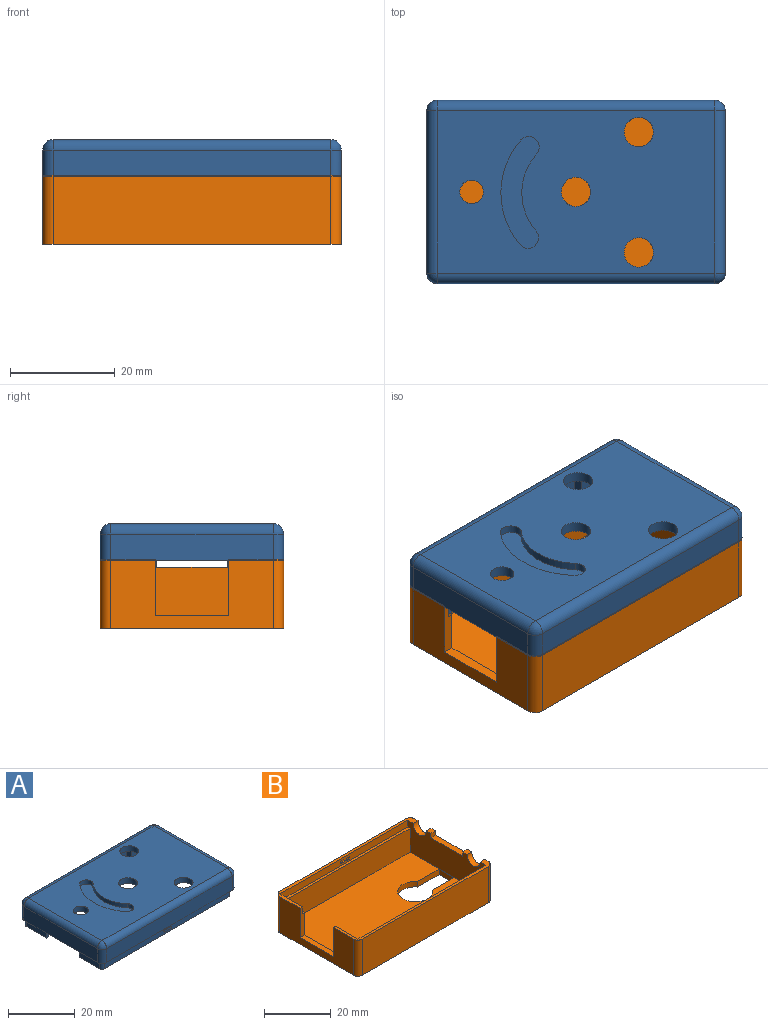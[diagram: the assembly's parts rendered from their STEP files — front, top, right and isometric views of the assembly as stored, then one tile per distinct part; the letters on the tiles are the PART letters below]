
ASSEMBLY  parts=2 mates=1
PART A: 108 faces, bbox 57x35x9.8 mm
  f0: plane 8.52x2.8mm, normal (-1,0,0), area 23.8mm2, adj f1,f6,f105,f106
  f1: plane 54.02x9.52mm, normal (0,0,-1), area 62.3mm2, adj f0,f2,f3,f4,f80,f105,f106
  f2: plane 8.52x2.8mm, normal (1,0,0), area 23.8mm2, adj f1,f4,f6,f106
  f3: plane 54.74x2.8mm, normal (0,-1,0), area 146.2mm2, adj f1,f6,f79,f80,f92,f99,f100,f101
  f4: plane 55.02x2.8mm, normal (0,1,0), area 148.4mm2, adj f1,f2,f6,f79,f80
  f5: plane 54.02x9.52mm, normal (0,0,-1), area 62.3mm2, adj f75,f76,f77,f78,f93,f104,f107
  f6: plane 57x35mm, normal (0,0,-1), area 165.2mm2, adj f0,f2,f3,f4,f7,f9,f10,f11
  f7: plane 8.1x5.03mm, normal (0,1,0), area 40.7mm2, adj f6,f8,f17,f73
  f8: plane 53x31mm, normal (0,0,-1), area 1497.2mm2, adj f7,f9,f14,f15,f16,f17,f23,f24
  f9: plane 37.41x5.03mm, normal (0,1,0), area 188.1mm2, adj f6,f8,f31,f71
  f10: plane 31x5.03mm, normal (-1,0,0), area 155.9mm2, adj f6,f81,f83,f84
  f11: plane 53x5.03mm, normal (0,1,0), area 266.5mm2, adj f6,f81,f85,f86
  f12: plane 53x5.03mm, normal (0,-1,0), area 266.5mm2, adj f6,f83,f89,f92
  f13: plane 31.01x5.04mm, normal (1,0,0), area 69.7mm2, adj f6,f18,f19,f20,f21,f27,f28,f29
  f14: plane 53x5.03mm, normal (0,-1,0), area 266.5mm2, adj f6,f8,f15,f17
  f15: plane 31x5.03mm, normal (1,0,0), area 155.9mm2, adj f6,f8,f14,f16
  f16: plane 5.03x0.48mm, normal (0,1,0), area 2.4mm2, adj f6,f8,f15,f32
  f17: plane 31x5.03mm, normal (-1,0,0), area 69.7mm2, adj f6,f7,f8,f14,f18,f19,f20,f21
  f18: cylinder r=2.75mm len=5.5mm, axis (1,0,0), area 17.8mm2, adj f6,f13,f17,f29
  f19: cylinder r=2.75mm len=5.5mm, axis (1,0,0), area 17.7mm2, adj f6,f13,f17,f28
  f20: plane 4.53x2mm, normal (0,1,0), area 9.1mm2, adj f13,f17,f27,f29
  f21: plane 4.53x2mm, normal (0,-1,0), area 9.1mm2, adj f13,f17,f27,f28
  f22: plane 53x31mm, normal (0,0,1), area 1464.7mm2, adj f23,f24,f25,f26,f55,f56,f57,f58
  f23: cylinder r=2.8mm len=5.6mm, axis (0,0,1), area 35.2mm2, adj f8,f22
  f24: cylinder r=2.8mm len=5.6mm, axis (0,0,1), area 35.2mm2, adj f8,f22
  f25: cylinder r=2.8mm len=5.6mm, axis (0,0,1), area 35.2mm2, adj f8,f22
  f26: cylinder r=2.25mm len=4.5mm, axis (0,0,1), area 28.3mm2, adj f8,f22
  f27: plane 13.5x2mm, normal (0,0,-1), area 27mm2, adj f13,f17,f20,f21
  f28: plane 2x1.87mm, normal (0,0,-1), area 3.7mm2, adj f13,f17,f19,f21
  f29: plane 2x1.88mm, normal (0,0,-1), area 3.8mm2, adj f13,f17,f18,f20
  f30: plane 3.5x1.77mm, normal (0,-1,0), area 6.2mm2, adj f6,f31,f32,f34
  f31: plane 6.8x2mm, normal (1,0,0), area 13.6mm2, adj f8,f9,f30,f33,f34
  f32: plane 6.8x2mm, normal (-1,0,0), area 13.6mm2, adj f8,f16,f30,f33,f34
  f33: plane 6.8x3.5mm, normal (0,1,0), area 23.8mm2, adj f8,f31,f32,f34
  f34: plane 3.5x2mm, normal (0,0,-1), area 7mm2, adj f30,f31,f32,f33
  f35: plane 6.8x2mm, normal (1,0,0), area 13.6mm2, adj f8,f36,f38,f39
  f36: plane 6.8x3.5mm, normal (0,-1,0), area 23.8mm2, adj f8,f35,f37,f39
  f37: plane 6.8x2mm, normal (-1,0,0), area 13.6mm2, adj f8,f36,f38,f39
  f38: plane 6.8x3.5mm, normal (0,1,0), area 23.8mm2, adj f8,f35,f37,f39
  f39: plane 3.5x2mm, normal (0,0,-1), area 7mm2, adj f35,f36,f37,f38
  f40: plane 6.8x2mm, normal (1,0,0), area 13.6mm2, adj f8,f41,f43,f44
  f41: plane 6.8x3.5mm, normal (0,-1,0), area 23.8mm2, adj f8,f40,f42,f44
  f42: plane 6.8x2mm, normal (-1,0,0), area 13.6mm2, adj f8,f41,f43,f44
  f43: plane 6.8x3.5mm, normal (0,1,0), area 23.8mm2, adj f8,f40,f42,f44
  f44: plane 3.5x2mm, normal (0,0,-1), area 7mm2, adj f40,f41,f42,f43
  f45: plane 6.8x2mm, normal (-1,0,0), area 13.6mm2, adj f8,f46,f48,f49
  f46: plane 6.8x3.5mm, normal (0,1,0), area 23.8mm2, adj f8,f45,f47,f49
  f47: plane 6.8x2mm, normal (1,0,0), area 13.6mm2, adj f8,f46,f48,f49
  f48: plane 6.8x3.5mm, normal (0,-1,0), area 23.8mm2, adj f8,f45,f47,f49
  f49: plane 3.5x2mm, normal (0,0,-1), area 7mm2, adj f45,f46,f47,f48
  f50: plane 6.8x3.5mm, normal (0,1,0), area 23.8mm2, adj f8,f51,f53,f54
  f51: plane 6.8x2mm, normal (1,0,0), area 13.6mm2, adj f8,f50,f52,f54
  f52: plane 6.8x3.5mm, normal (0,-1,0), area 23.8mm2, adj f8,f51,f53,f54
  f53: plane 6.8x2mm, normal (-1,0,0), area 13.6mm2, adj f8,f50,f52,f54
  f54: plane 3.5x2mm, normal (0,0,-1), area 7mm2, adj f50,f51,f52,f53
  f55: cylinder r=11.14mm len=14.73mm, axis (0,0,1), area 24.1mm2, adj f22,f56,f58,f59
  f56: cylinder r=2mm len=3.49mm, axis (0,0,1), area 9.4mm2, adj f22,f55,f57,f59
  f57: cylinder r=15.14mm len=20.02mm, axis (0,0,1), area 32.8mm2, adj f22,f56,f58,f59
  f58: cylinder r=2mm len=3.51mm, axis (0,0,1), area 9.4mm2, adj f22,f55,f57,f59
  f59: plane 21.37x7.34mm, normal (0,0,1), area 88.5mm2, adj f55,f56,f57,f58
  f60: plane 6.8x2mm, normal (-1,0,0), area 13.6mm2, adj f8,f61,f63,f64
  f61: plane 6.8x3.5mm, normal (0,1,0), area 23.8mm2, adj f8,f60,f62,f64
  f62: plane 6.8x2mm, normal (1,0,0), area 13.6mm2, adj f8,f61,f63,f64
  f63: plane 6.8x3.5mm, normal (0,-1,0), area 23.8mm2, adj f8,f60,f62,f64
  f64: plane 3.5x2mm, normal (0,0,-1), area 7mm2, adj f60,f61,f62,f63
  f65: plane 6.8x2mm, normal (-1,0,0), area 13.6mm2, adj f8,f66,f68,f69
  f66: plane 6.8x3.5mm, normal (0,1,0), area 23.8mm2, adj f8,f65,f67,f69
  f67: plane 6.8x2mm, normal (1,0,0), area 13.6mm2, adj f8,f66,f68,f69
  f68: plane 6.8x3.5mm, normal (0,-1,0), area 23.8mm2, adj f8,f65,f67,f69
  f69: plane 3.5x2mm, normal (0,0,-1), area 7mm2, adj f65,f66,f67,f68
  f70: plane 3.5x1.77mm, normal (0,-1,0), area 6.2mm2, adj f6,f71,f73,f74
  f71: plane 6.8x2mm, normal (-1,0,0), area 13.6mm2, adj f8,f9,f70,f72,f74
  f72: plane 6.8x3.5mm, normal (0,1,0), area 23.8mm2, adj f8,f71,f73,f74
  f73: plane 6.8x2mm, normal (1,0,0), area 13.6mm2, adj f7,f8,f70,f72,f74
  f74: plane 3.5x2mm, normal (0,0,-1), area 7mm2, adj f70,f71,f72,f73
  f75: plane 53.02x2.8mm, normal (0,1,0), area 146.1mm2, adj f5,f6,f93,f94,f95,f96,f97,f104
  f76: plane 53.02x2.8mm, normal (0,-1,0), area 148.4mm2, adj f5,f6,f77,f93
  f77: plane 8.52x2.8mm, normal (1,0,0), area 23.8mm2, adj f5,f6,f76,f107
  f78: plane 8.52x2.8mm, normal (-1,0,0), area 23.8mm2, adj f5,f6,f104,f107
  f79: plane 2.01x1.01mm, normal (0,0,-1), area 1.9mm2, adj f3,f4,f80,f92
  f80: plane 2.77x1mm, normal (1,0,0), area 2.8mm2, adj f1,f3,f4,f79
  f81: cylinder r=2mm len=5.03mm, axis (0,0,-1), area 15.8mm2, adj f6,f10,f11,f82
  f82: sphere r=2mm, area 6.3mm2, adj f81,f84,f85
  f83: cylinder r=2mm len=5.03mm, axis (0,0,1), area 15.8mm2, adj f6,f10,f12,f87
  f84: cylinder r=2mm len=31mm, axis (0,1,0), area 97.4mm2, adj f10,f22,f82,f87
  f85: cylinder r=2mm len=53mm, axis (1,0,0), area 166.5mm2, adj f11,f22,f82,f88
  f86: cylinder r=2mm len=5.03mm, axis (0,0,1), area 15.8mm2, adj f6,f11,f13,f88
  f87: sphere r=2mm, area 8.6mm2, adj f83,f84,f89
  f88: sphere r=2mm, area 6.3mm2, adj f85,f86,f90
  f89: cylinder r=2mm len=53mm, axis (-1,0,0), area 166.5mm2, adj f12,f22,f87,f91
  f90: cylinder r=2mm len=31mm, axis (0,-1,0), area 97.4mm2, adj f13,f22,f88,f91
  f91: sphere r=2mm, area 4mm2, adj f89,f90,f92
  f92: cylinder r=2mm len=5.05mm, axis (0,0,-1), area 15.8mm2, adj f3,f6,f12,f13,f79,f91
  f93: plane 2.8x1mm, normal (1,0,0), area 2.8mm2, adj f5,f6,f75,f76
  f94: plane 0.75x0.3mm, normal (1,0,0), area 0.2mm2, adj f75,f95,f97,f98
  f95: plane 3x0.3mm, normal (0,0,-1), area 0.9mm2, adj f75,f94,f96,f98
  f96: plane 0.75x0.3mm, normal (-1,0,0), area 0.2mm2, adj f75,f95,f97,f98
  f97: plane 3x0.3mm, normal (0,0,1), area 0.9mm2, adj f75,f94,f96,f98
  f98: plane 3x0.75mm, normal (0,1,0), area 2.2mm2, adj f94,f95,f96,f97
  f99: plane 0.75x0.3mm, normal (-1,0,0), area 0.2mm2, adj f3,f100,f102,f103
  f100: plane 3x0.3mm, normal (0,0,-1), area 0.9mm2, adj f3,f99,f101,f103
  f101: plane 0.75x0.3mm, normal (1,0,0), area 0.2mm2, adj f3,f100,f102,f103
  f102: plane 3x0.3mm, normal (0,0,1), area 0.9mm2, adj f3,f99,f101,f103
  f103: plane 3x0.75mm, normal (0,-1,0), area 2.3mm2, adj f99,f100,f101,f102
  f104: cylinder r=1mm len=2.8mm, axis (0,0,-1), area 4.4mm2, adj f5,f6,f75,f78
  f105: cylinder r=1mm len=2.8mm, axis (0,0,-1), area 4.4mm2, adj f0,f1,f3,f6
  f106: plane 2.8x1mm, normal (0,1,0), area 2.8mm2, adj f0,f1,f2,f6
  f107: plane 2.8x1mm, normal (0,-1,0), area 2.8mm2, adj f5,f6,f77,f78
PART B: 46 faces, bbox 57x35x13.2 mm
  f0: plane 54x2.5mm, normal (0,-1,0), area 131.5mm2, adj f5,f8,f28,f29,f41,f42,f43,f44
  f1: plane 54x2.5mm, normal (0,1,0), area 131.5mm2, adj f3,f8,f30,f31,f36,f37,f38,f39
  f2: plane 10.75x2mm, normal (0,1,0), area 19mm2, adj f3,f7,f13,f23,f30,f31
  f3: plane 57x10.5mm, normal (0,0,1), area 69.5mm2, adj f1,f2,f7,f8,f9,f11,f16,f30
  f4: plane 10.75x2mm, normal (0,-1,0), area 19mm2, adj f5,f7,f13,f23,f28,f29
  f5: plane 57x10.5mm, normal (0,0,1), area 69.5mm2, adj f0,f4,f7,f8,f10,f11,f15,f28
  f6: plane 57x35mm, normal (0,0,-1), area 1852.5mm2, adj f7,f9,f10,f11,f24,f25,f26,f27
  f7: plane 31x13.23mm, normal (-1,0,0), area 259.6mm2, adj f2,f3,f4,f5,f6,f23,f33,f34
  f8: plane 33x11.23mm, normal (-1,0,0), area 307.4mm2, adj f0,f1,f3,f5,f12,f14,f15,f16
  f9: plane 53x13.23mm, normal (0,-1,0), area 701.1mm2, adj f3,f6,f32,f33
  f10: plane 53x13.23mm, normal (0,1,0), area 701.1mm2, adj f5,f6,f34,f35
  f11: plane 31x13.23mm, normal (1,0,0), area 364.4mm2, adj f3,f5,f6,f15,f16,f17,f18,f20
  f12: plane 53x8.73mm, normal (0,1,0), area 462.6mm2, adj f8,f13,f19,f31
  f13: plane 31x8.73mm, normal (1,0,0), area 155.1mm2, adj f2,f4,f12,f14,f19,f23,f29,f31
  f14: plane 53x8.73mm, normal (0,-1,0), area 462.6mm2, adj f8,f13,f19,f29
  f15: cylinder r=2.75mm len=5.5mm, axis (1,0,0), area 17.8mm2, adj f5,f8,f11,f22
  f16: cylinder r=2.75mm len=5.5mm, axis (1,0,0), area 17.7mm2, adj f3,f8,f11,f21
  f17: plane 2x1.53mm, normal (0,-1,0), area 3.1mm2, adj f8,f11,f20,f22
  f18: plane 2x1.53mm, normal (0,1,0), area 3.1mm2, adj f8,f11,f20,f21
  f19: plane 53x31mm, normal (0,0,1), area 1503.9mm2, adj f8,f12,f13,f14,f24,f25,f26,f27
  f20: plane 13.5x2mm, normal (0,0,1), area 27mm2, adj f8,f11,f17,f18
  f21: plane 2x1.87mm, normal (0,0,1), area 3.7mm2, adj f8,f11,f16,f18
  f22: plane 2x1.88mm, normal (0,0,1), area 3.8mm2, adj f8,f11,f15,f17
  f23: plane 14x2mm, normal (0,0,1), area 28mm2, adj f2,f4,f7,f13
  f24: cylinder r=5.25mm len=10.5mm, axis (0,0,1), area 52.5mm2, adj f6,f19,f25,f26
  f25: plane 9.05x2mm, normal (0,-1,0), area 18.1mm2, adj f6,f19,f24,f27
  f26: plane 9.05x2mm, normal (0,1,0), area 18.1mm2, adj f6,f19,f24,f27
  f27: plane 6.3x2mm, normal (-1,0,0), area 12.6mm2, adj f6,f19,f25,f26
  f28: plane 9.5x2.5mm, normal (1,0,0), area 23.8mm2, adj f0,f4,f5,f29
  f29: plane 54x9.5mm, normal (0,0,1), area 62.5mm2, adj f0,f4,f8,f13,f14,f28
  f30: plane 9.5x2.5mm, normal (1,0,0), area 23.8mm2, adj f1,f2,f3,f31
  f31: plane 54x9.5mm, normal (0,0,1), area 62.5mm2, adj f1,f2,f8,f12,f13,f30
  f32: cylinder r=2mm len=13.23mm, axis (0,0,-1), area 41.6mm2, adj f3,f6,f9,f11
  f33: cylinder r=2mm len=13.23mm, axis (0,0,1), area 41.6mm2, adj f3,f6,f7,f9
  f34: cylinder r=2mm len=13.23mm, axis (0,0,-1), area 41.6mm2, adj f5,f6,f7,f10
  f35: cylinder r=2mm len=13.23mm, axis (0,0,1), area 41.6mm2, adj f5,f6,f10,f11
  f36: plane 1x0.4mm, normal (1,0,0), area 0.4mm2, adj f1,f37,f39,f40
  f37: plane 3.5x0.4mm, normal (0,0,-1), area 1.4mm2, adj f1,f36,f38,f40
  f38: plane 1x0.4mm, normal (-1,0,0), area 0.4mm2, adj f1,f37,f39,f40
  f39: plane 3.5x0.4mm, normal (0,0,1), area 1.4mm2, adj f1,f36,f38,f40
  f40: plane 3.5x1mm, normal (0,1,0), area 3.5mm2, adj f36,f37,f38,f39
  f41: plane 1x0.4mm, normal (-1,0,0), area 0.4mm2, adj f0,f42,f44,f45
  f42: plane 3.5x0.4mm, normal (0,0,-1), area 1.4mm2, adj f0,f41,f43,f45
  f43: plane 1x0.4mm, normal (1,0,0), area 0.4mm2, adj f0,f42,f44,f45
  f44: plane 3.5x0.4mm, normal (0,0,1), area 1.4mm2, adj f0,f41,f43,f45
  f45: plane 3.5x1mm, normal (0,-1,0), area 3.5mm2, adj f41,f42,f43,f44
PLACE A rot(axis=(-1,0,0),0deg) t=(10.29,14.57,20.33)mm
PLACE B t=(10.29,14.57,20.6)mm fixed
MATE fastened B.f16 <-> A.f18  axis (1,0,0) through (38.79,3.2,15.04)mm
